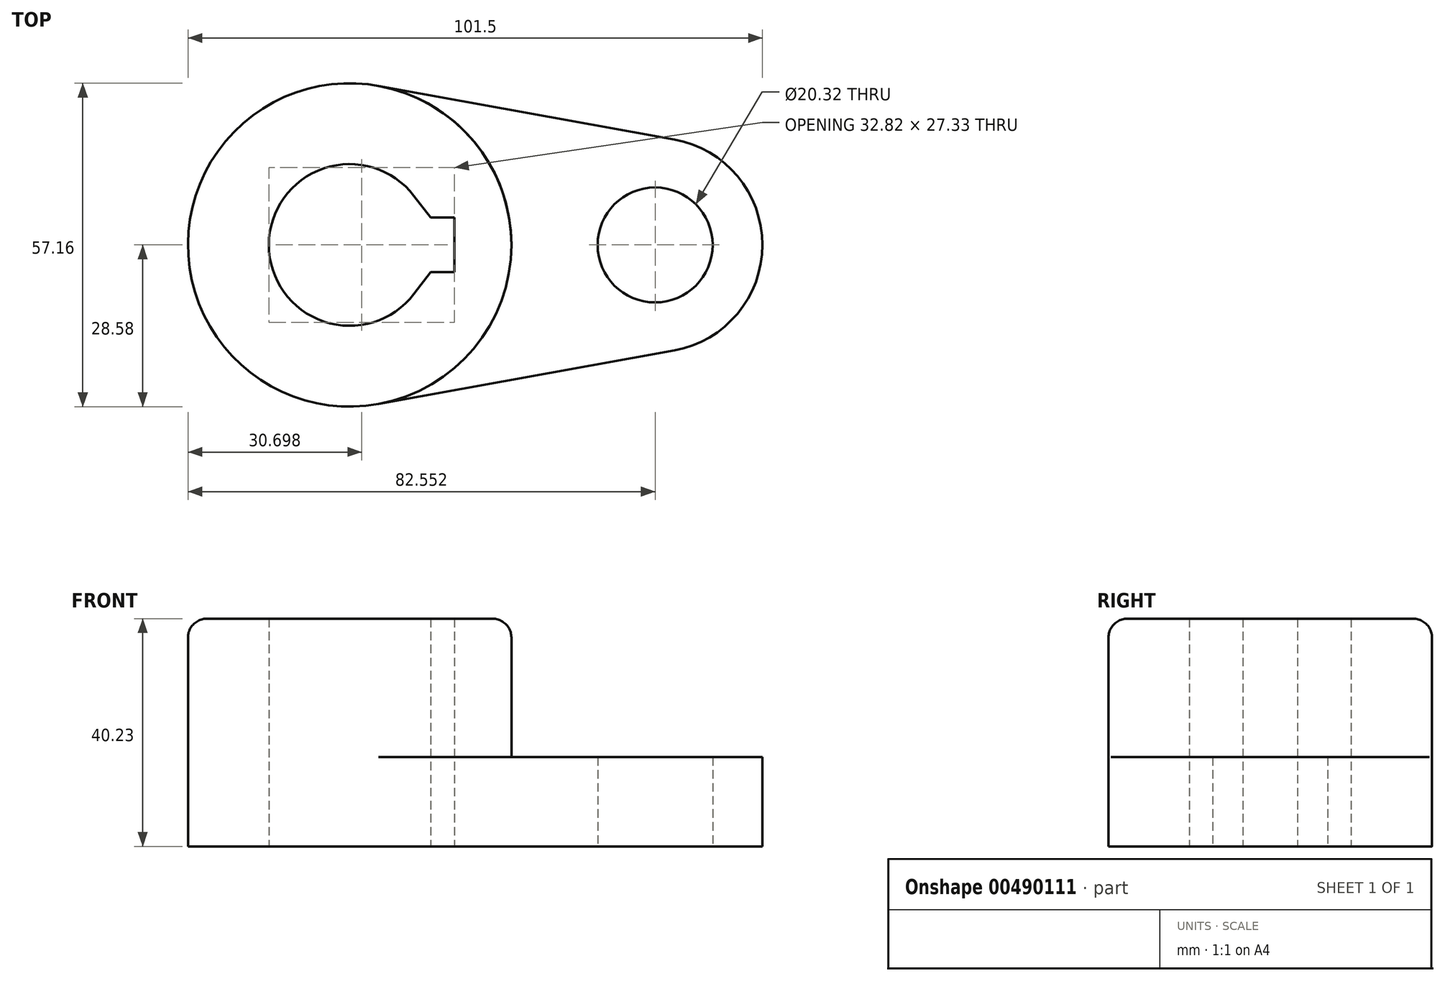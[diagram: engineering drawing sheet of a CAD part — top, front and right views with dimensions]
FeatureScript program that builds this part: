
annotation { "Feature Type Name" : "Feature", "Feature Type Description" : "" }
export const myFeature = defineFeature(function(context is Context, id is Id, definition is map)
    precondition{}
    {
        {
            var Q0;
            Q0=qCreatedBy(makeId("Top.planeOp"),FACE);
            var sketch = newSketch(context, id + "F0", { "sketchPlane" : qUnion([Q0])});
            skCircle(sketch, "E0", {"center": v(-47.84, 0) * mm, "radius": 28.58 * mm});
            skCircle(sketch, "E1", {"center": v(6.13, 0) * mm, "radius": 10.16 * mm});
            skArc(sketch, "E2", {"start": v(6.13, -18.94) * mm, "mid": v(25.08, 0) * mm, "end": v(6.13, 18.94) * mm});
            skLineSegment(sketch, "E3", {"start": v(-42.74, 28.12) * mm, "end": v(9.51, 18.64) * mm});
            skLineSegment(sketch, "E4", {"start": v(-42.74, -28.12) * mm, "end": v(9.51, -18.64) * mm});
            skArc(sketch, "E5", {"start": v(-36.48, 8.66) * mm, "mid": v(-62.13, 0) * mm, "end": v(-36.48, -8.66) * mm});
            skPoint(sketch, "E6", {"position": v(-33.56, 0) * mm});
            skPoint(sketch, "E7", {"position": v(-29.31, 0) * mm});
            skPoint(sketch, "E8", {"position": v(-29.31, 4.83) * mm});
            skPoint(sketch, "E9", {"position": v(-29.31, -4.83) * mm});
            skPoint(sketch, "E10", {"position": v(-33.56, -4.83) * mm});
            skPoint(sketch, "E11", {"position": v(-33.56, 4.83) * mm});
            skLineSegment(sketch, "E12", {"start": v(-33.56, -4.83) * mm, "end": v(-29.31, -4.83) * mm});
            skLineSegment(sketch, "E13", {"start": v(-33.56, 4.83) * mm, "end": v(-29.31, 4.83) * mm});
            skLineSegment(sketch, "E14", {"start": v(-29.31, 0) * mm, "end": v(-29.31, -4.83) * mm});
            skLineSegment(sketch, "E15", {"start": v(-29.31, 4.83) * mm, "end": v(-29.31, 0) * mm});
            skLineSegment(sketch, "E16", {"start": v(-36.48, 8.66) * mm, "end": v(-33.56, 4.83) * mm});
            skLineSegment(sketch, "E17", {"start": v(-36.48, -8.66) * mm, "end": v(-33.56, -4.83) * mm});
            skSolve(sketch);
        }
        {
            var Q0;
            Q0=makeQuery(id+"F0.imprint","IMPRINT",FACE,{"disambiguationData":[TD([[makeQuery(id+"F0.imprint","IMPRINT",EDGE,{"derivedFrom":sQuery(id+"F0.wireOp",EDGE,"E1")}),-1.0]])]});
            extrude(context, id + "F1", {"entities" : qUnion([Q0]), "depth" : 15.77 * mm});
        }
        {
            var Q0;
            Q0=makeQuery(id+"F0.imprint","IMPRINT",FACE,{"disambiguationData":[TD([[makeQuery(id+"F0.imprint","IMPRINT",EDGE,{"derivedFrom":sQuery(id+"F0.wireOp",EDGE,"E5")}),-1.0]])]});
            extrude(context, id + "F2", {"entities" : qUnion([Q0]), "operationType" : NewBodyOperationType.ADD, "depth" : 40.23 * mm});
        }
        {
            var Q0;
            Q0=makeQuery(id+"F2.opExtrude","CAP_EDGE",EDGE,{"disambiguationData":[OSD([sQuery(id+"F0.wireOp",EDGE,"E0")])],"isStart":false});
            fillet(context, id + "F3", {"entities" : qUnion([Q0]), "radius" : 3.3 * mm, "tangentPropagation" : true, "allowEdgeOverflow" : false});
        }
    });
